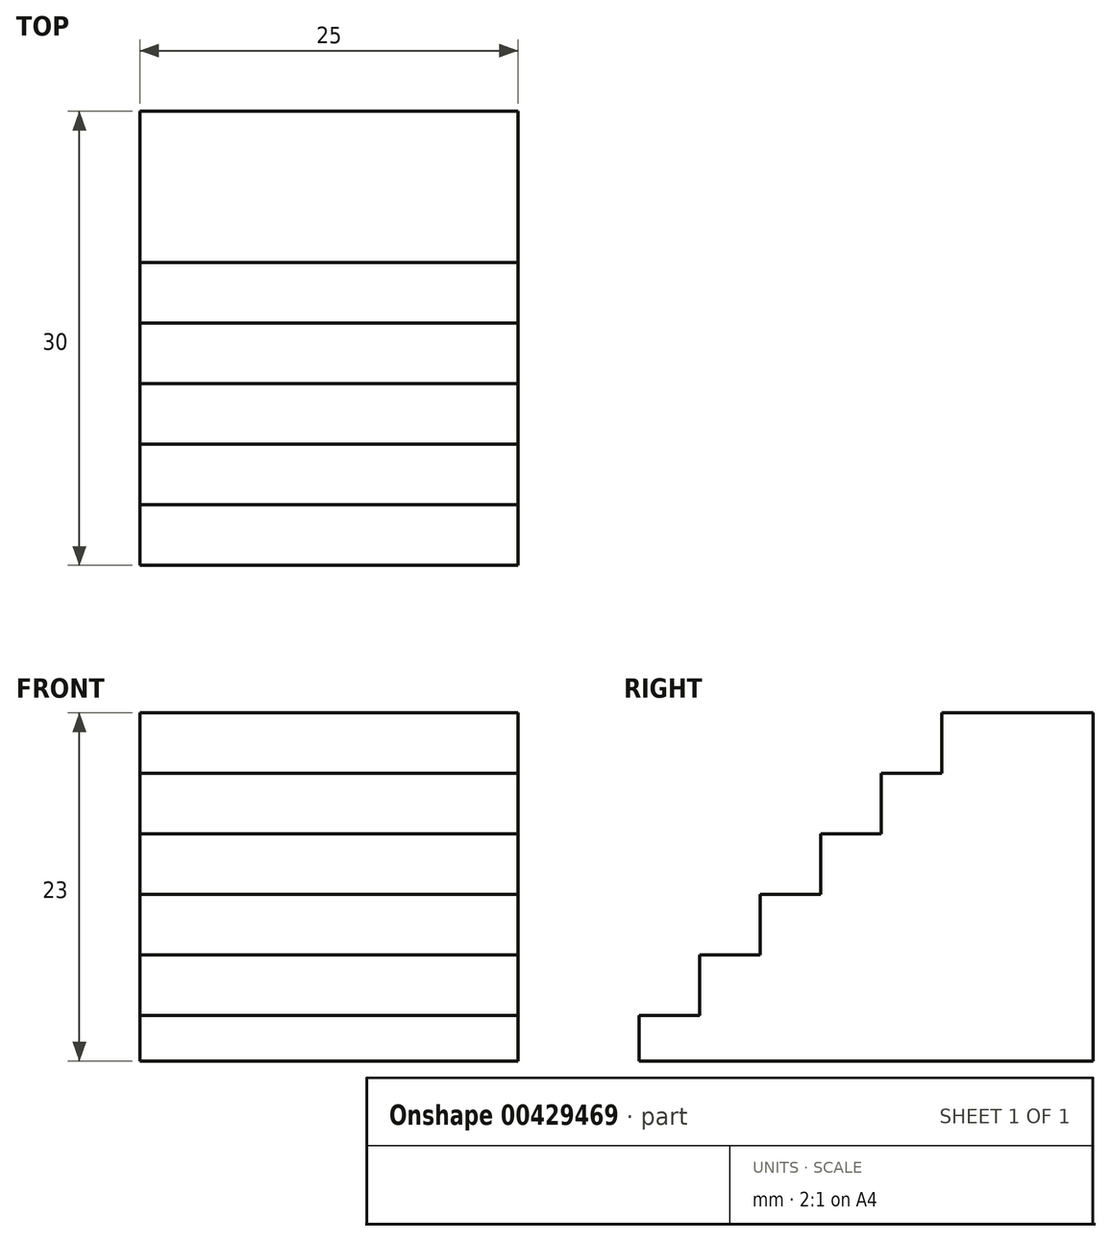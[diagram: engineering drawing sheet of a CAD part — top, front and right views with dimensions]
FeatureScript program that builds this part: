
annotation { "Feature Type Name" : "Feature", "Feature Type Description" : "" }
export const myFeature = defineFeature(function(context is Context, id is Id, definition is map)
    precondition{}
    {
        {
            var Q0;
            Q0=qCreatedBy(makeId("Front.planeOp"),FACE);
            var sketch = newSketch(context, id + "F0", { "sketchPlane" : qUnion([Q0])});
            skLineSegment(sketch, "E0.bottom", {"start": v(0, 0) * mm, "end": v(25, 0) * mm});
            skLineSegment(sketch, "E0.top", {"start": v(0, 23) * mm, "end": v(25, 23) * mm});
            skLineSegment(sketch, "E0.left", {"start": v(0, 0) * mm, "end": v(0, 23) * mm});
            skLineSegment(sketch, "E0.right", {"start": v(25, 0) * mm, "end": v(25, 23) * mm});
            skSolve(sketch);
        }
        {
            var Q0;
            Q0 = qSketchRegion(id + "F0", true);
            extrude(context, id + "F1", {"entities" : qUnion([Q0]), "oppositeDirection" : true, "depth" : 30 * mm});
        }
        {
            var Q0;
            Q0=makeQuery(id+"F1.opExtrude","SWEPT_FACE",FACE,{"disambiguationData":[OSD([sQuery(id+"F0.wireOp",EDGE,"E0.right")])]});
            var sketch = newSketch(context, id + "F2", { "sketchPlane" : qUnion([Q0])});
            skLineSegment(sketch, "E1", {"start": v(0, 23) * mm, "end": v(0, 3) * mm});
            skLineSegment(sketch, "E2", {"start": v(0, 3) * mm, "end": v(4, 3) * mm});
            skLineSegment(sketch, "E3", {"start": v(4, 3) * mm, "end": v(4, 7) * mm});
            skLineSegment(sketch, "E4", {"start": v(4, 7) * mm, "end": v(8, 7) * mm});
            skLineSegment(sketch, "E5", {"start": v(8, 7) * mm, "end": v(8, 11) * mm});
            skLineSegment(sketch, "E6", {"start": v(8, 11) * mm, "end": v(12, 11) * mm});
            skLineSegment(sketch, "E7", {"start": v(12, 11) * mm, "end": v(12, 15) * mm});
            skLineSegment(sketch, "E8", {"start": v(12, 15) * mm, "end": v(16, 15) * mm});
            skLineSegment(sketch, "E9", {"start": v(16, 15) * mm, "end": v(16, 19) * mm});
            skLineSegment(sketch, "E10", {"start": v(16, 19) * mm, "end": v(20, 19) * mm});
            skLineSegment(sketch, "E11", {"start": v(20, 19) * mm, "end": v(20, 23) * mm});
            skLineSegment(sketch, "E12", {"start": v(20, 23) * mm, "end": v(0, 23) * mm});
            skSolve(sketch);
        }
        {
            var Q0;
            Q0 = qSketchRegion(id + "F2", true);
            extrude(context, id + "F3", {"entities" : qUnion([Q0]), "operationType" : NewBodyOperationType.REMOVE, "endBound" : BoundingType.THROUGH_ALL, "oppositeDirection" : true, "depth" : 25 * mm});
        }
    });
